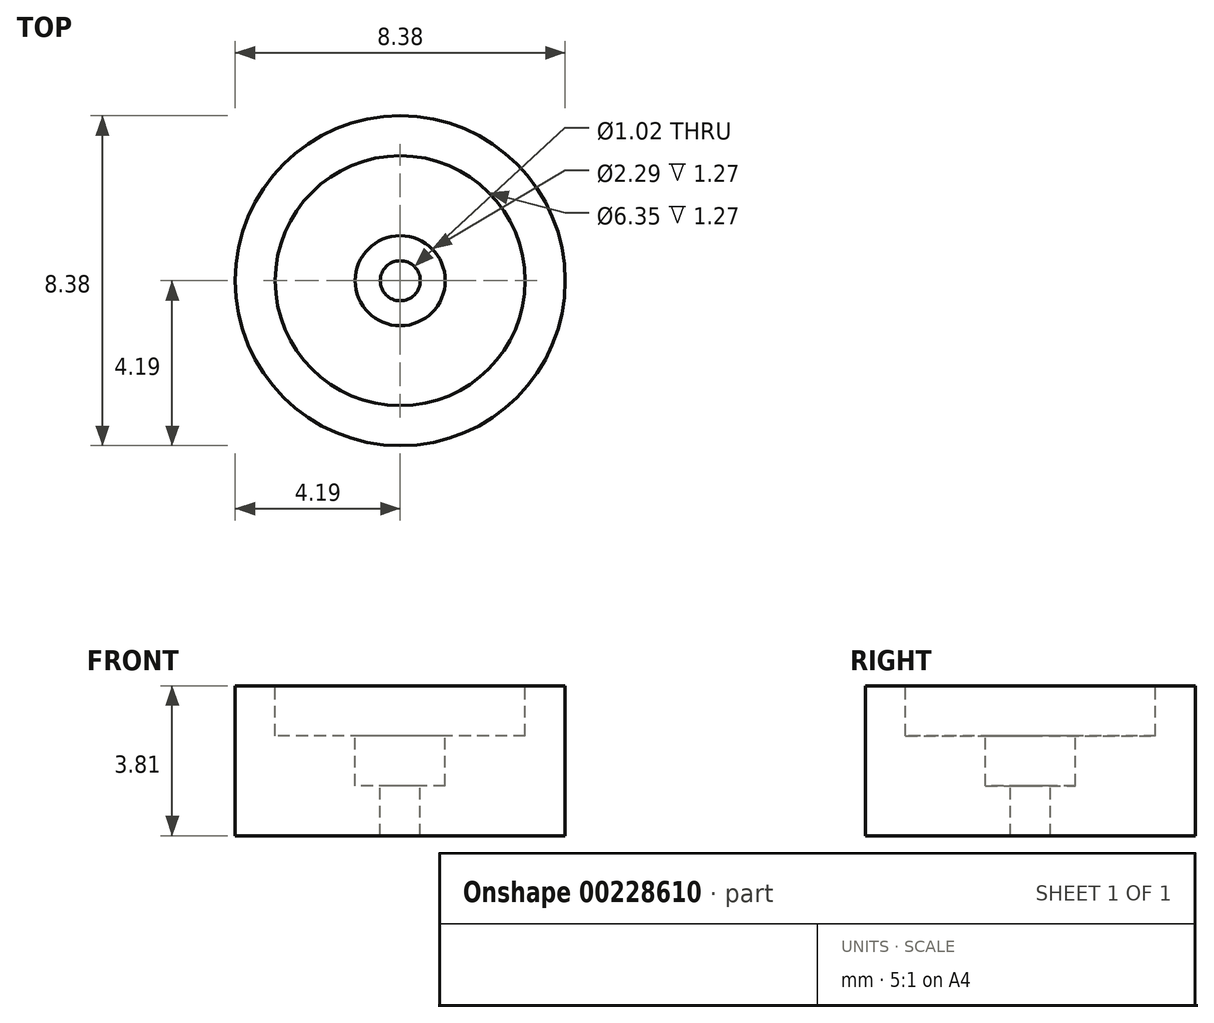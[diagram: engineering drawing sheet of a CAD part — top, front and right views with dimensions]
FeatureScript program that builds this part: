
annotation { "Feature Type Name" : "Feature", "Feature Type Description" : "" }
export const myFeature = defineFeature(function(context is Context, id is Id, definition is map)
    precondition{}
    {
        {
            var Q0;
            Q0=qCreatedBy(makeId("Front.planeOp"),FACE);
            var sketch = newSketch(context, id + "F0", { "sketchPlane" : qUnion([Q0])});
            skLineSegment(sketch, "E0", {"start": v(-0.5, -2.54) * mm, "end": v(-4.2, -2.54) * mm});
            skLineSegment(sketch, "E1", {"start": v(-4.2, -2.54) * mm, "end": v(-4.2, 1.27) * mm});
            skLineSegment(sketch, "E2", {"start": v(-4.2, 1.27) * mm, "end": v(-3.18, 1.27) * mm});
            skLineSegment(sketch, "E3", {"start": v(-3.18, 1.27) * mm, "end": v(-3.18, 0) * mm});
            skLineSegment(sketch, "E4", {"start": v(-3.18, 0) * mm, "end": v(-1.14, 0) * mm});
            skLineSegment(sketch, "E5", {"start": v(-0.5, -1.27) * mm, "end": v(-0.5, -2.54) * mm});
            skLineSegment(sketch, "E6", {"start": v(0, 1.74) * mm, "end": v(0, -2.85) * mm, "construction": true});
            skLineSegment(sketch, "E7", {"start": v(-1.14, 0) * mm, "end": v(-1.14, -1.27) * mm});
            skLineSegment(sketch, "E8", {"start": v(-1.14, -1.27) * mm, "end": v(-0.5, -1.27) * mm});
            skPoint(sketch, "E9.orphan", {"position": v(-0.5, 0) * mm});
            skSolve(sketch);
        }
        {
            var Q0;
            Q0 = qSketchRegion(id + "F0", true);
            var Q1;
            Q1=sQuery(id+"F0.wireOp",EDGE,"E6");
            revolve(context, id + "F1", {"entities" : qUnion([Q0]), "axis" : qUnion([Q1]), "revolveType" : RevolveType.FULL});
        }
    });
